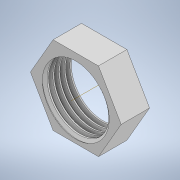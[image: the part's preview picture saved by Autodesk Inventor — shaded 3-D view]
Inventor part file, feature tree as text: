
AUTODESK INVENTOR PART (.ipt)
format: ipt  version: 2021.1 (Build 251245010, 245A)  size: 330,752 bytes
history: native  units: in
note: dims shown in document units (in); Inventor stores cm internally (conversion verified against a paired STEP export)
features: sketch x3, extrude x2, helix x1
ambient origin geometry x8: Origin, YZ Plane, XZ Plane, XY Plane, X Axis, Y Axis, Z Axis, Center Point
bodies: Solid1 (feature_tree)
feature tree (6):
  extrude  "Extrusion1"  Depth=0.5in
  helix  "Coil1"  [1 undecoded]
  extrude  "Extrusion2"  TaperAngle=60.0deg  [1 undecoded]
  sketch  "Sketch1"  dims[d0=1.1327in d1=0.125in d2=0.5in d3=0.0in]
  sketch  "Sketch2"  dims[d4=0.0072in d5=60.0deg]
  sketch  "Sketch3"  dims[d7=120.0deg d8=0.0072in d9=60.0deg d10=120.0deg d11=0.1in d12=0.05in d13=0.5664in d15=0.1in d16=0.7in d17=0.3937in d18=0.0in d19=90.0deg d20=90.0deg d21=0.0in d22=0.0in d23=0.5in d24=0.0in d25=0.6236in]
note: 2 required parameter values undecoded (feature->parameter linkage not recoverable at this tier; creation-order binding heuristic only, values carry confidence <= 0.55)
